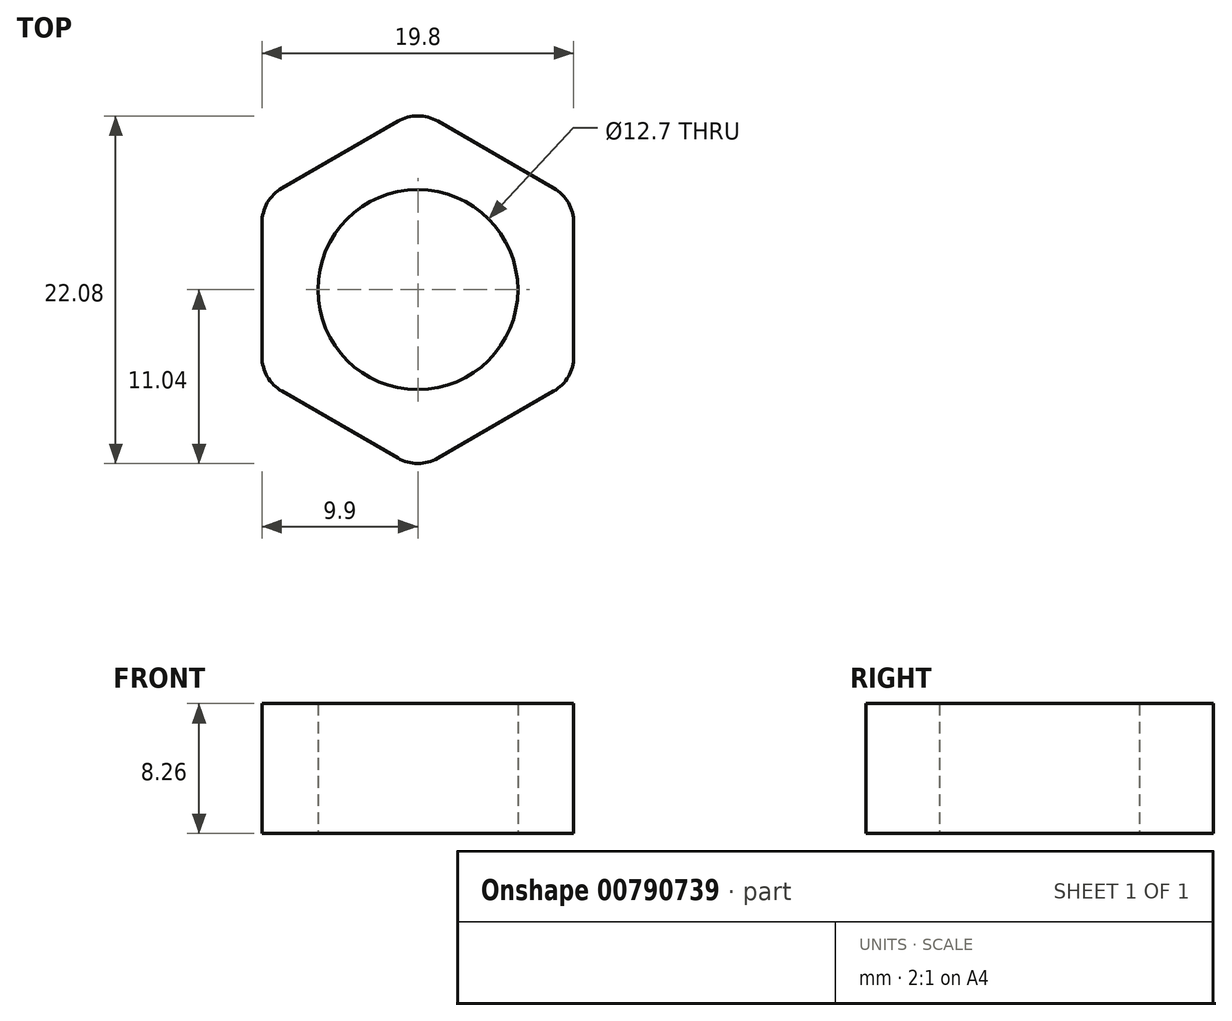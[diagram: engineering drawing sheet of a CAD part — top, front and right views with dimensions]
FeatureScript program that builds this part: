
annotation { "Feature Type Name" : "Feature", "Feature Type Description" : "" }
export const myFeature = defineFeature(function(context is Context, id is Id, definition is map)
    precondition{}
    {
        {
            var Q0;
            Q0=qCreatedBy(makeId("Top.planeOp"),FACE);
            var sketch = newSketch(context, id + "F0", { "sketchPlane" : qUnion([Q0])});
            skCircle(sketch, "E0.cCircle", {"center": v(0, 0) * mm, "radius": 11.43 * mm, "construction": true});
            skLineSegment(sketch, "E0.0", {"start": v(0, 11.43) * mm, "end": v(9.9, 5.72) * mm});
            skLineSegment(sketch, "E0.1", {"start": v(9.9, 5.72) * mm, "end": v(9.9, -5.71) * mm});
            skLineSegment(sketch, "E0.2", {"start": v(9.9, -5.71) * mm, "end": v(0, -11.43) * mm});
            skLineSegment(sketch, "E0.3", {"start": v(0, -11.43) * mm, "end": v(-9.9, -5.72) * mm});
            skLineSegment(sketch, "E0.4", {"start": v(-9.9, -5.72) * mm, "end": v(-9.9, 5.71) * mm});
            skLineSegment(sketch, "E0.5", {"start": v(-9.9, 5.71) * mm, "end": v(0, 11.43) * mm});
            skCircle(sketch, "E1", {"center": v(0, 0) * mm, "radius": 6.35 * mm});
            skSolve(sketch);
        }
        {
            var Q0;
            Q0=makeQuery(id+"F0.imprint","IMPRINT",FACE,{"disambiguationData":[TD([[makeQuery(id+"F0.imprint","IMPRINT",EDGE,{"derivedFrom":sQuery(id+"F0.wireOp",EDGE,"E0.0")}),-1.0]])]});
            extrude(context, id + "F1", {"entities" : qUnion([Q0]), "depth" : 8.25 * mm, "offsetDistance" : 25.4 * mm});
        }
        {
            var Q0;
            Q0=makeQuery(id+"F1.opExtrude","SWEPT_EDGE",EDGE,{"disambiguationData":[OSD([sQuery(id+"F0.wireOp",EDGE,"E0.3"),sQuery(id+"F0.wireOp",EDGE,"E0.4")])]});
            var Q1;
            Q1=makeQuery(id+"F1.opExtrude","SWEPT_EDGE",EDGE,{"disambiguationData":[OSD([sQuery(id+"F0.wireOp",EDGE,"E0.2"),sQuery(id+"F0.wireOp",EDGE,"E0.3")])]});
            var Q2;
            Q2=makeQuery(id+"F1.opExtrude","SWEPT_EDGE",EDGE,{"disambiguationData":[OSD([sQuery(id+"F0.wireOp",EDGE,"E0.1"),sQuery(id+"F0.wireOp",EDGE,"E0.2")])]});
            var Q3;
            Q3=makeQuery(id+"F1.opExtrude","SWEPT_EDGE",EDGE,{"disambiguationData":[OSD([sQuery(id+"F0.wireOp",EDGE,"E0.0"),sQuery(id+"F0.wireOp",EDGE,"E0.1")])]});
            var Q4;
            Q4=makeQuery(id+"F1.opExtrude","SWEPT_EDGE",EDGE,{"disambiguationData":[OSD([sQuery(id+"F0.wireOp",EDGE,"E0.0"),sQuery(id+"F0.wireOp",EDGE,"E0.5")])]});
            var Q5;
            Q5=makeQuery(id+"F1.opExtrude","SWEPT_EDGE",EDGE,{"disambiguationData":[OSD([sQuery(id+"F0.wireOp",EDGE,"E0.4"),sQuery(id+"F0.wireOp",EDGE,"E0.5")])]});
            fillet(context, id + "F2", {"entities" : qUnion([Q0, Q1, Q2, Q3, Q4, Q5]), "radius" : 2.54 * mm, "tangentPropagation" : true, "allowEdgeOverflow" : false});
        }
    });
